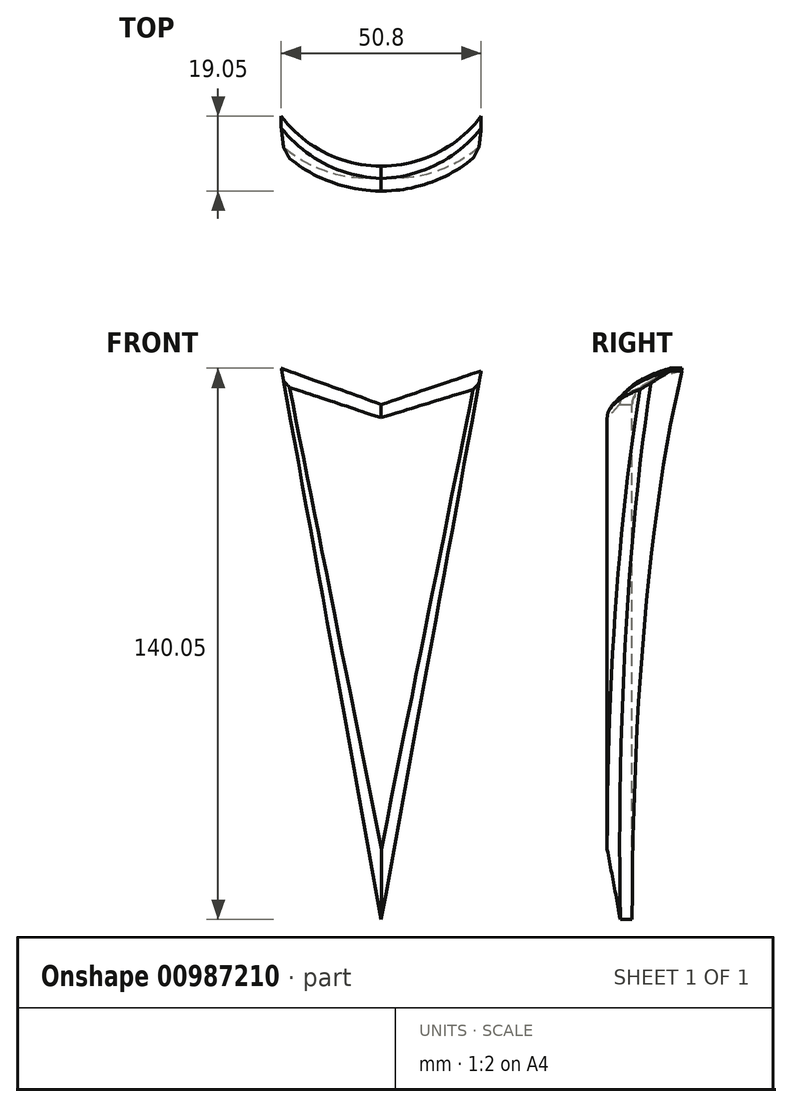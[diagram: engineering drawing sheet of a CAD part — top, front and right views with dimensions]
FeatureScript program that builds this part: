
annotation { "Feature Type Name" : "Feature", "Feature Type Description" : "" }
export const myFeature = defineFeature(function(context is Context, id is Id, definition is map)
    precondition{}
    {
        {
            var Q0;
            Q0=qCreatedBy(makeId("Front.planeOp"),FACE);
            var sketch = newSketch(context, id + "F0", { "sketchPlane" : qUnion([Q0])});
            skLineSegment(sketch, "E0", {"start": v(0, -69.85) * mm, "end": v(25.4, 69.53) * mm});
            skLineSegment(sketch, "E1", {"start": v(0, -69.85) * mm, "end": v(-25.4, 70.2) * mm});
            skLineSegment(sketch, "E2", {"start": v(25.4, 69.53) * mm, "end": v(0, 60.97) * mm});
            skLineSegment(sketch, "E3", {"start": v(0, 60.97) * mm, "end": v(-25.4, 70.2) * mm});
            skLineSegment(sketch, "E4", {"start": v(-25.4, 70.2) * mm, "end": v(25.4, 69.53) * mm});
            skSolve(sketch);
        }
        {
            var Q0;
            Q0=makeQuery(id+"F0.imprint","IMPRINT",FACE,{"disambiguationData":[TD([[makeQuery(id+"F0.imprint","IMPRINT",EDGE,{"derivedFrom":sQuery(id+"F0.wireOp",EDGE,"E0")}),1.0]])]});
            extrude(context, id + "F1", {"entities" : qUnion([Q0]), "depth" : 19.05 * mm, "offsetDistance" : 25.4 * mm});
        }
        {
            var Q0;
            Q0=qCreatedBy(makeId("Top.planeOp"),FACE);
            cPlane(context, id + "F2", {"entities" : qUnion([Q0]), "cplaneType" : CPlaneType.OFFSET, "offset" : 76.2 * mm, "width" : 152.4 * mm, "height" : 152.4 * mm});
        }
        {
            var Q0;
            Q0=qCreatedBy(id+"F2.planeOp",FACE);
            var sketch = newSketch(context, id + "F3", { "sketchPlane" : qUnion([Q0])});
            skArc(sketch, "E5", {"start": v(-25.4, 0) * mm, "mid": v(0, -12.7) * mm, "end": v(25.4, 0) * mm});
            skLineSegment(sketch, "E6", {"start": v(-25.4, 0) * mm, "end": v(25.4, 0) * mm});
            skSolve(sketch);
        }
        {
            var Q0;
            Q0 = qSketchRegion(id + "F3", true);
            extrude(context, id + "F4", {"entities" : qUnion([Q0]), "operationType" : NewBodyOperationType.REMOVE, "endBound" : BoundingType.THROUGH_ALL, "oppositeDirection" : true, "depth" : 25.4 * mm, "offsetDistance" : 25.4 * mm});
        }
        {
            var Q0;
            Q0=qCreatedBy(id+"F2.planeOp",FACE);
            var sketch = newSketch(context, id + "F5", { "sketchPlane" : qUnion([Q0])});
            skLineSegment(sketch, "E7", {"start": v(-25.4, 0) * mm, "end": v(-25.4, -8.9) * mm});
            skLineSegment(sketch, "E8", {"start": v(25.4, 0) * mm, "end": v(25.4, -8.9) * mm});
            skArc(sketch, "E9", {"start": v(-25.4, -8.89) * mm, "mid": v(0, -19.05) * mm, "end": v(25.4, -8.9) * mm});
            skLineSegment(sketch, "E10", {"start": v(-25.4, 0) * mm, "end": v(25.4, 0) * mm});
            skLineSegment(sketch, "E11", {"start": v(-25.4, -8.9) * mm, "end": v(-25.4, -19.05) * mm});
            skPoint(sketch, "E11.endSnap0", {"position": v(0, -19.05) * mm});
            skLineSegment(sketch, "E12", {"start": v(-25.4, -19.05) * mm, "end": v(0, -19.05) * mm});
            skLineSegment(sketch, "E13", {"start": v(0, -19.05) * mm, "end": v(25.4, -19.05) * mm});
            skLineSegment(sketch, "E14", {"start": v(25.4, -19.05) * mm, "end": v(25.4, -8.9) * mm});
            skSolve(sketch);
        }
        {
            var Q0;
            {var subQ0=sQuery(id+"F5.wireOp",EDGE,"E11");Q0=makeQuery(id+"F5.imprint","IMPRINT",FACE,{"disambiguationData":[TD([[makeQuery(id+"F5.imprint","IMPRINT",EDGE,{"derivedFrom":subQ0}),1.0]])]});}
            var Q1;
            {var subQ2=sQuery(id+"F5.wireOp",EDGE,"E13");Q1=makeQuery(id+"F5.imprint","IMPRINT",FACE,{"disambiguationData":[TD([[makeQuery(id+"F5.imprint","IMPRINT",EDGE,{"derivedFrom":subQ2}),1.0]])]});}
            extrude(context, id + "F6", {"entities" : qUnion([Q0, Q1]), "operationType" : NewBodyOperationType.REMOVE, "endBound" : BoundingType.THROUGH_ALL, "oppositeDirection" : true, "depth" : 25.4 * mm, "offsetDistance" : 25.4 * mm});
        }
        {
            var Q0;
            {var subQ0=sQuery(id+"F5.wireOp",EDGE,"E9");Q0=makeQuery(id+"F6.boolean.opBoolean","INTERSECT",EDGE,{"derivedFrom":[makeQuery(id+"F1.opExtrude","SWEPT_FACE",FACE,{"disambiguationData":[OSD([sQuery(id+"F0.wireOp",EDGE,"E1")])]}),makeQuery(id+"F6.opExtrude","SWEPT_FACE",FACE,{"disambiguationData":[OSD([subQ0]),TDD([makeQuery(id+"F5.imprint","IMPRINT",EDGE,{"disambiguationData":[TD([[makeQuery(id+"F5.imprint","INTERSECT",VERTEX,{"derivedFrom":[sQuery(id+"F5.wireOp",EDGE,"E7"),subQ0,sQuery(id+"F5.wireOp",EDGE,"E11")]}),-1.0]])],"derivedFrom":subQ0})])]})]});}
            var Q1;
            {var subQ0=sQuery(id+"F5.wireOp",EDGE,"E9");Q1=makeQuery(id+"F6.boolean.opBoolean","INTERSECT",EDGE,{"derivedFrom":[makeQuery(id+"F1.opExtrude","SWEPT_FACE",FACE,{"disambiguationData":[OSD([sQuery(id+"F0.wireOp",EDGE,"E0")])]}),makeQuery(id+"F6.opExtrude","SWEPT_FACE",FACE,{"disambiguationData":[OSD([subQ0]),TDD([makeQuery(id+"F5.imprint","IMPRINT",EDGE,{"disambiguationData":[TD([[makeQuery(id+"F5.imprint","INTERSECT",VERTEX,{"derivedFrom":[sQuery(id+"F5.wireOp",EDGE,"E7"),subQ0,sQuery(id+"F5.wireOp",EDGE,"E11")]}),-1.0]])],"derivedFrom":subQ0})])]}),makeQuery(id+"F6.opExtrude","SWEPT_FACE",FACE,{"disambiguationData":[OSD([subQ0]),TDD([makeQuery(id+"F5.imprint","IMPRINT",EDGE,{"disambiguationData":[TD([[makeQuery(id+"F5.imprint","INTERSECT",VERTEX,{"derivedFrom":[sQuery(id+"F5.wireOp",EDGE,"E8"),subQ0,sQuery(id+"F5.wireOp",EDGE,"E14")]}),1.0]])],"derivedFrom":subQ0})])]})]});}
            var Q2;
            {var subQ0=sQuery(id+"F5.wireOp",EDGE,"E9");Q2=makeQuery(id+"F6.boolean.opBoolean","INTERSECT",EDGE,{"derivedFrom":[makeQuery(id+"F1.opExtrude","SWEPT_FACE",FACE,{"disambiguationData":[OSD([sQuery(id+"F0.wireOp",EDGE,"E2")])]}),makeQuery(id+"F6.opExtrude","SWEPT_FACE",FACE,{"disambiguationData":[OSD([subQ0]),TDD([makeQuery(id+"F5.imprint","IMPRINT",EDGE,{"disambiguationData":[TD([[makeQuery(id+"F5.imprint","INTERSECT",VERTEX,{"derivedFrom":[sQuery(id+"F5.wireOp",EDGE,"E7"),subQ0,sQuery(id+"F5.wireOp",EDGE,"E11")]}),-1.0]])],"derivedFrom":subQ0})])]}),makeQuery(id+"F6.opExtrude","SWEPT_FACE",FACE,{"disambiguationData":[OSD([subQ0]),TDD([makeQuery(id+"F5.imprint","IMPRINT",EDGE,{"disambiguationData":[TD([[makeQuery(id+"F5.imprint","INTERSECT",VERTEX,{"derivedFrom":[sQuery(id+"F5.wireOp",EDGE,"E8"),subQ0,sQuery(id+"F5.wireOp",EDGE,"E14")]}),1.0]])],"derivedFrom":subQ0})])]})]});}
            var Q3;
            {var subQ0=sQuery(id+"F5.wireOp",EDGE,"E9");Q3=makeQuery(id+"F6.boolean.opBoolean","INTERSECT",EDGE,{"derivedFrom":[makeQuery(id+"F1.opExtrude","SWEPT_FACE",FACE,{"disambiguationData":[OSD([sQuery(id+"F0.wireOp",EDGE,"E3")])]}),makeQuery(id+"F6.opExtrude","SWEPT_FACE",FACE,{"disambiguationData":[OSD([subQ0]),TDD([makeQuery(id+"F5.imprint","IMPRINT",EDGE,{"disambiguationData":[TD([[makeQuery(id+"F5.imprint","INTERSECT",VERTEX,{"derivedFrom":[sQuery(id+"F5.wireOp",EDGE,"E7"),subQ0,sQuery(id+"F5.wireOp",EDGE,"E11")]}),-1.0]])],"derivedFrom":subQ0})])]})]});}
            chamfer(context, id + "F7", {"entities" : qUnion([Q0, Q1, Q2, Q3]), "width" : 3.17 * mm, "tangentPropagation" : true});
        }
    });
